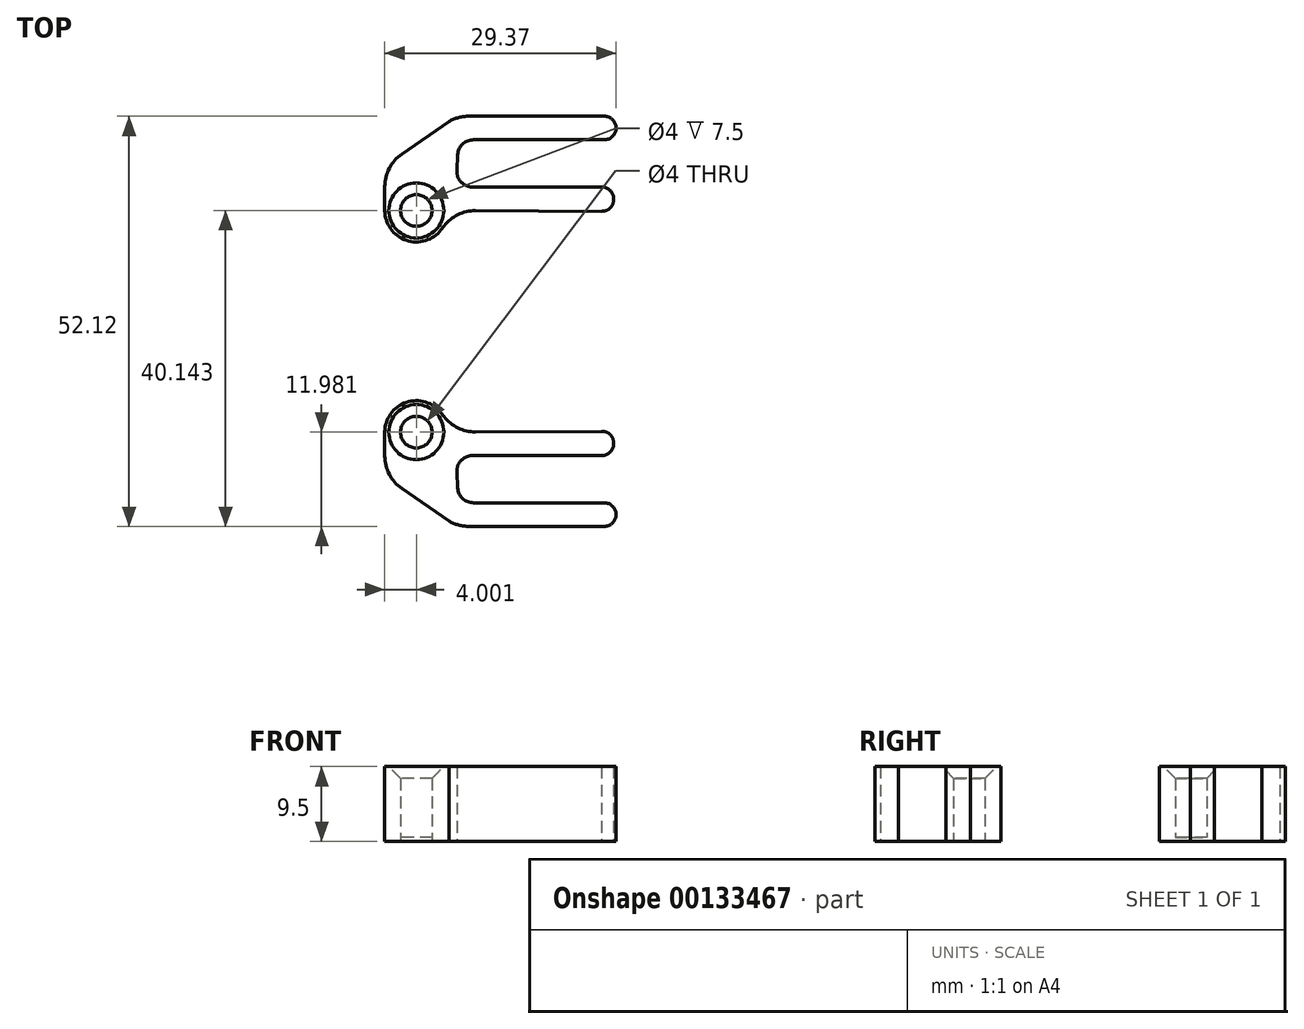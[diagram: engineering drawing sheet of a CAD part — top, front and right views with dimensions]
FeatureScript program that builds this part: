
annotation { "Feature Type Name" : "Feature", "Feature Type Description" : "" }
export const myFeature = defineFeature(function(context is Context, id is Id, definition is map)
    precondition{}
    {
        {
            var Q0;
            Q0=qCreatedBy(makeId("Top.planeOp"),FACE);
            var sketch = newSketch(context, id + "F0", { "sketchPlane" : qUnion([Q0])});
            skLineSegment(sketch, "E0.bottom", {"start": v(8.37, -3) * mm, "end": v(-8.05, -3) * mm});
            skLineSegment(sketch, "E0.top", {"start": v(8.67, 3) * mm, "end": v(-7.94, 3) * mm});
            skLineSegment(sketch, "E0.right", {"start": v(-10.05, -0.89) * mm, "end": v(-9.94, 1.11) * mm});
            skPoint(sketch, "E0.middle", {"position": v(0, 0) * mm});
            skLineSegment(sketch, "E1", {"start": v(10.17, 4.5) * mm, "end": v(10.17, 4.5) * mm});
            skLineSegment(sketch, "E2", {"start": v(8.67, 6) * mm, "end": v(-8.52, 6) * mm});
            skLineSegment(sketch, "E3", {"start": v(9.87, -4.55) * mm, "end": v(9.87, -4.46) * mm});
            skPoint(sketch, "E4.visualSharp", {"position": v(-9.83, 3) * mm});
            skArc(sketch, "E4.filletArc", {"start": v(-7.94, 3) * mm, "mid": v(-9.31, 2.45) * mm, "end": v(-9.94, 1.11) * mm});
            skPoint(sketch, "E5.visualSharp", {"position": v(-10.17, -3) * mm});
            skArc(sketch, "E5.filletArc", {"start": v(-10.05, -0.89) * mm, "mid": v(-9.5, -2.37) * mm, "end": v(-8.05, -3) * mm});
            skPoint(sketch, "E6.visualSharp", {"position": v(10.17, 3) * mm});
            skArc(sketch, "E6.filletArc", {"start": v(8.67, 3) * mm, "mid": v(9.73, 3.44) * mm, "end": v(10.17, 4.5) * mm});
            skPoint(sketch, "E7.visualSharp", {"position": v(10.17, 6) * mm});
            skArc(sketch, "E7.filletArc", {"start": v(10.17, 4.5) * mm, "mid": v(9.73, 5.56) * mm, "end": v(8.67, 6) * mm});
            skPoint(sketch, "E8.visualSharp", {"position": v(9.83, -3) * mm});
            skArc(sketch, "E8.filletArc", {"start": v(9.87, -4.46) * mm, "mid": v(9.42, -3.43) * mm, "end": v(8.37, -3) * mm});
            skPoint(sketch, "E9", {"position": v(-9.83, 6) * mm});
            skCircle(sketch, "E10", {"center": v(-15.2, -5.98) * mm, "radius": 4 * mm});
            skCircle(sketch, "E11", {"center": v(-15.2, -5.98) * mm, "radius": 2 * mm});
            skPoint(sketch, "E12.visualSharp", {"position": v(9.9, -6) * mm});
            skArc(sketch, "E12.filletArc", {"start": v(8.34, -6.09) * mm, "mid": v(9.44, -5.64) * mm, "end": v(9.87, -4.55) * mm});
            skArc(sketch, "E13.filletArc", {"start": v(-8.52, 6) * mm, "mid": v(-9.83, 5.82) * mm, "end": v(-11.05, 5.31) * mm});
            skLineSegment(sketch, "E14.trimOffspring", {"start": v(-7.7, -6.01) * mm, "end": v(8.34, -6.09) * mm});
            skLineSegment(sketch, "E15", {"start": v(-19.2, -5.98) * mm, "end": v(-19.2, -2.94) * mm});
            skLineSegment(sketch, "E16", {"start": v(-11.05, 5.31) * mm, "end": v(-17.04, 1.17) * mm});
            skPoint(sketch, "E17.visualSharp", {"position": v(-19.2, -0.32) * mm});
            skArc(sketch, "E17.filletArc", {"start": v(-17.04, 1.17) * mm, "mid": v(-18.63, -0.62) * mm, "end": v(-19.2, -2.94) * mm});
            skLineSegment(sketch, "E18", {"start": v(-11.68, -7.96) * mm, "end": v(-12.03, -8.42) * mm});
            skPoint(sketch, "E19.visualSharp", {"position": v(-10.17, -6) * mm});
            skArc(sketch, "E19.filletArc", {"start": v(-7.7, -6.01) * mm, "mid": v(-9.91, -6.52) * mm, "end": v(-11.68, -7.96) * mm});
            skLineSegment(sketch, "E20", {"start": v(-30.3, -20.06) * mm, "end": v(36.63, -20.06) * mm, "construction": true});
            skCircle(sketch, "E21.MirrorC", {"center": v(-15.2, -34.14) * mm, "radius": 4 * mm});
            skCircle(sketch, "E22.MirrorC", {"center": v(-15.2, -34.14) * mm, "radius": 2 * mm});
            skLineSegment(sketch, "E23.MirrorCS", {"start": v(-11.68, -32.15) * mm, "end": v(-12.03, -31.7) * mm});
            skArc(sketch, "E24.MirrorCS", {"start": v(-7.7, -34.1) * mm, "mid": v(-9.91, -33.6) * mm, "end": v(-11.68, -32.15) * mm});
            skLineSegment(sketch, "E25.MirrorCS", {"start": v(-7.7, -34.1) * mm, "end": v(8.34, -34.03) * mm});
            skArc(sketch, "E26.MirrorCS", {"start": v(8.34, -34.03) * mm, "mid": v(9.44, -34.47) * mm, "end": v(9.87, -35.57) * mm});
            skArc(sketch, "E27.MirrorCS", {"start": v(9.87, -35.65) * mm, "mid": v(9.42, -36.69) * mm, "end": v(8.37, -37.12) * mm});
            skLineSegment(sketch, "E28.MirrorCS", {"start": v(8.37, -37.12) * mm, "end": v(-8.05, -37.12) * mm});
            skArc(sketch, "E29.MirrorCS", {"start": v(-10.05, -39.23) * mm, "mid": v(-9.5, -37.74) * mm, "end": v(-8.05, -37.12) * mm});
            skLineSegment(sketch, "E30.MirrorCS", {"start": v(-10.05, -39.23) * mm, "end": v(-9.94, -41.23) * mm});
            skArc(sketch, "E31.MirrorCS", {"start": v(-7.94, -43.12) * mm, "mid": v(-9.31, -42.57) * mm, "end": v(-9.94, -41.23) * mm});
            skLineSegment(sketch, "E32.MirrorCS", {"start": v(8.67, -43.12) * mm, "end": v(-7.94, -43.12) * mm});
            skArc(sketch, "E33.MirrorCS", {"start": v(8.67, -43.12) * mm, "mid": v(9.73, -43.55) * mm, "end": v(10.17, -44.62) * mm});
            skArc(sketch, "E34.MirrorCS", {"start": v(10.17, -44.62) * mm, "mid": v(9.73, -45.68) * mm, "end": v(8.67, -46.12) * mm});
            skLineSegment(sketch, "E35.MirrorCS", {"start": v(8.67, -46.12) * mm, "end": v(-8.52, -46.12) * mm});
            skArc(sketch, "E36.MirrorCS", {"start": v(-8.52, -46.12) * mm, "mid": v(-9.83, -45.94) * mm, "end": v(-11.05, -45.43) * mm});
            skLineSegment(sketch, "E37.MirrorCS", {"start": v(-11.05, -45.43) * mm, "end": v(-17.04, -41.29) * mm});
            skArc(sketch, "E38.MirrorCS", {"start": v(-17.04, -41.29) * mm, "mid": v(-18.63, -39.5) * mm, "end": v(-19.2, -37.17) * mm});
            skLineSegment(sketch, "E39.MirrorCS", {"start": v(-19.2, -34.14) * mm, "end": v(-19.2, -37.17) * mm});
            skLineSegment(sketch, "E40.MirrorCS", {"start": v(9.87, -35.57) * mm, "end": v(9.87, -35.65) * mm});
            skSolve(sketch);
        }
        {
            var Q0;
            Q0 = qSketchRegion(id + "F0", true);
            extrude(context, id + "F1", {"entities" : qUnion([Q0]), "depth" : 9 * mm});
        }
        {
            var Q0;
            Q0=makeQuery(id+"F0.imprint","IMPRINT",FACE,{"disambiguationData":[TD([[makeQuery(id+"F0.imprint","IMPRINT",EDGE,{"derivedFrom":sQuery(id+"F0.wireOp",EDGE,"E0.bottom")}),1.0]])]});
            var Q1;
            Q1=makeQuery(id+"F0.imprint","IMPRINT",FACE,{"disambiguationData":[TD([[makeQuery(id+"F0.imprint","IMPRINT",EDGE,{"derivedFrom":sQuery(id+"F0.wireOp",EDGE,"E11")}),-1.0]])]});
            var Q2;
            Q2=makeQuery(id+"F0.imprint","IMPRINT",FACE,{"disambiguationData":[TD([[makeQuery(id+"F0.imprint","IMPRINT",EDGE,{"derivedFrom":sQuery(id+"F0.wireOp",EDGE,"E11")}),1.0]])]});
            extrude(context, id + "F2", {"entities" : qUnion([Q0, Q1, Q2]), "operationType" : NewBodyOperationType.ADD, "oppositeDirection" : true, "depth" : .5 * mm});
        }
        {
            var Q0;
            Q0=makeQuery(id+"F1.opExtrude","CAP_FACE",FACE,{"disambiguationData":[OSD([sQuery(id+"F0.wireOp",EDGE,"E21.MirrorC"),sQuery(id+"F0.wireOp",EDGE,"E22.MirrorC"),sQuery(id+"F0.wireOp",EDGE,"E23.MirrorCS"),sQuery(id+"F0.wireOp",EDGE,"E24.MirrorCS"),sQuery(id+"F0.wireOp",EDGE,"E25.MirrorCS"),sQuery(id+"F0.wireOp",EDGE,"E26.MirrorCS"),sQuery(id+"F0.wireOp",EDGE,"E27.MirrorCS"),sQuery(id+"F0.wireOp",EDGE,"E28.MirrorCS"),sQuery(id+"F0.wireOp",EDGE,"E29.MirrorCS"),sQuery(id+"F0.wireOp",EDGE,"E30.MirrorCS"),sQuery(id+"F0.wireOp",EDGE,"E31.MirrorCS"),sQuery(id+"F0.wireOp",EDGE,"E32.MirrorCS"),sQuery(id+"F0.wireOp",EDGE,"E33.MirrorCS"),sQuery(id+"F0.wireOp",EDGE,"E34.MirrorCS"),sQuery(id+"F0.wireOp",EDGE,"E35.MirrorCS"),sQuery(id+"F0.wireOp",EDGE,"E36.MirrorCS"),sQuery(id+"F0.wireOp",EDGE,"E37.MirrorCS"),sQuery(id+"F0.wireOp",EDGE,"E38.MirrorCS"),sQuery(id+"F0.wireOp",EDGE,"E39.MirrorCS"),sQuery(id+"F0.wireOp",EDGE,"E40.MirrorCS")])],"isStart":true});
            var Q1;
            Q1=makeQuery(id+"F0.imprint","IMPRINT",FACE,{"disambiguationData":[TD([[makeQuery(id+"F0.imprint","IMPRINT",EDGE,{"derivedFrom":sQuery(id+"F0.wireOp",EDGE,"E22.MirrorC")}),-1.0]])]});
            extrude(context, id + "F3", {"entities" : qUnion([Q0, Q1]), "operationType" : NewBodyOperationType.ADD, "depth" : .5 * mm});
        }
        {
            var Q0;
            Q0=makeQuery(id+"F1.opExtrude","CAP_EDGE",EDGE,{"disambiguationData":[OSD([sQuery(id+"F0.wireOp",EDGE,"qKSuOZSO-lCXu-roR6-3C1M-0qSaArhSuQGC")])],"isStart":false});
            var Q1;
            Q1=makeQuery(id+"F1.opExtrude","CAP_EDGE",EDGE,{"disambiguationData":[OSD([sQuery(id+"F0.wireOp",EDGE,"E11")])],"isStart":false});
            var Q2;
            Q2=makeQuery(id+"F1.opExtrude","CAP_EDGE",EDGE,{"disambiguationData":[OSD([sQuery(id+"F0.wireOp",EDGE,"E22.MirrorC")])],"isStart":false});
            chamfer(context, id + "F4", {"entities" : qUnion([Q0, Q1, Q2]), "width" : 1.5 * mm, "tangentPropagation" : true});
        }
    });
